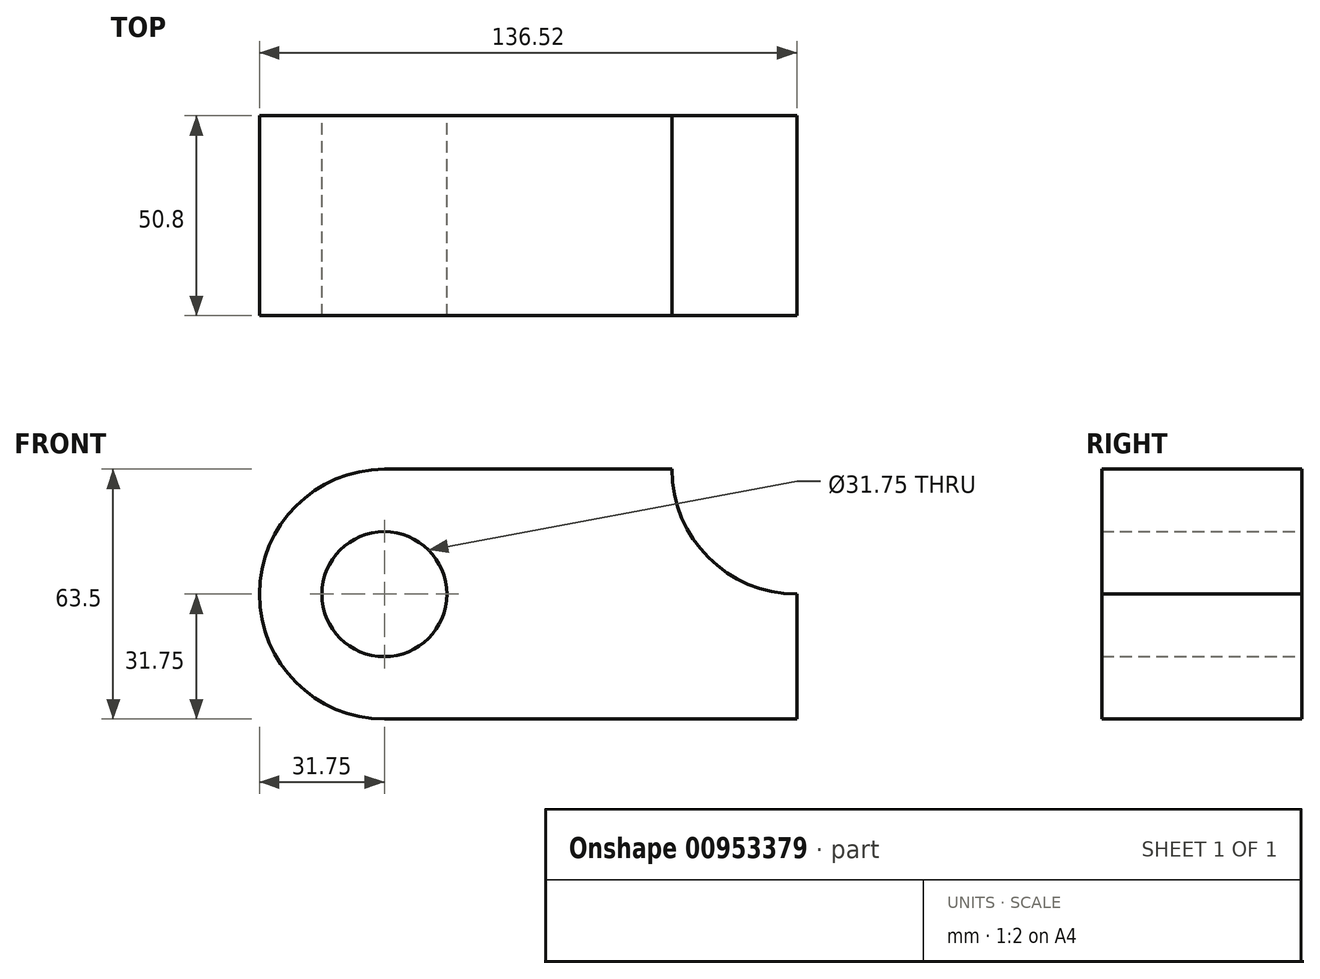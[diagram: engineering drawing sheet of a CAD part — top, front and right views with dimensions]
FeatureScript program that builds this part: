
annotation { "Feature Type Name" : "Feature", "Feature Type Description" : "" }
export const myFeature = defineFeature(function(context is Context, id is Id, definition is map)
    precondition{}
    {
        {
            var Q0;
            Q0=qCreatedBy(makeId("Front.planeOp"),FACE);
            var sketch = newSketch(context, id + "F0", { "sketchPlane" : qUnion([Q0])});
            skLineSegment(sketch, "E0", {"start": v(104.78, 0) * mm, "end": v(0, 0) * mm});
            skLineSegment(sketch, "E1", {"start": v(0, 31.75) * mm, "end": v(0, 0) * mm});
            skLineSegment(sketch, "E2", {"start": v(0, 31.75) * mm, "end": v(0, 63.5) * mm});
            skLineSegment(sketch, "E3", {"start": v(0, 63.5) * mm, "end": v(73.03, 63.5) * mm});
            skArc(sketch, "E4", {"start": v(73.03, 63.5) * mm, "mid": v(82.32, 41.05) * mm, "end": v(104.78, 31.75) * mm});
            skLineSegment(sketch, "E5", {"start": v(104.78, 31.75) * mm, "end": v(104.78, 0) * mm});
            skArc(sketch, "E6", {"start": v(0, 63.5) * mm, "mid": v(-31.75, 31.75) * mm, "end": v(0, 0) * mm});
            skCircle(sketch, "E7", {"center": v(0, 31.75) * mm, "radius": 15.88 * mm});
            skSolve(sketch);
        }
        {
            var Q0;
            Q0 = qSketchRegion(id + "F0", true);
            extrude(context, id + "F1", {"entities" : qUnion([Q0]), "depth" : 50.8 * mm, "offsetDistance" : 25.4 * mm});
        }
    });
